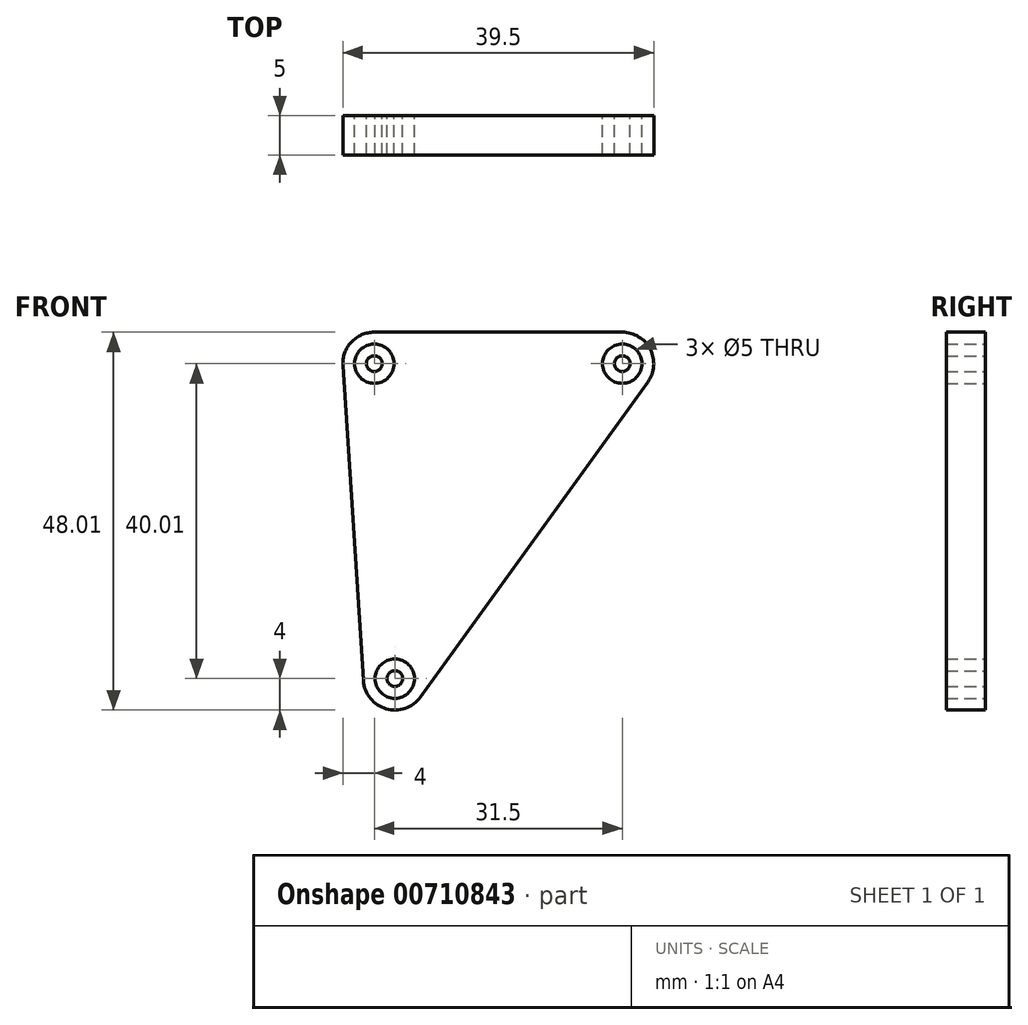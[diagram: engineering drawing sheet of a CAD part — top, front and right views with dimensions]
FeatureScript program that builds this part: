
annotation { "Feature Type Name" : "Feature", "Feature Type Description" : "" }
export const myFeature = defineFeature(function(context is Context, id is Id, definition is map)
    precondition{}
    {
        {
            var Q0;
            Q0=qCreatedBy(makeId("Front.planeOp"),FACE);
            var sketch = newSketch(context, id + "F0", { "sketchPlane" : qUnion([Q0])});
            skCircle(sketch, "E0", {"center": v(-5.7, 2.74) * mm, "radius": 2.5 * mm});
            skCircle(sketch, "E1", {"center": v(25.79, 2.74) * mm, "radius": 2.5 * mm});
            skCircle(sketch, "E2", {"center": v(-3.1, -37.27) * mm, "radius": 2.5 * mm});
            skArc(sketch, "E3", {"start": v(-5.7, 6.74) * mm, "mid": v(-8.63, 5.47) * mm, "end": v(-9.7, 2.48) * mm});
            skArc(sketch, "E4", {"start": v(29.03, 0.4) * mm, "mid": v(29.35, 4.56) * mm, "end": v(25.79, 6.74) * mm});
            skArc(sketch, "E5", {"start": v(-7.1, -37.53) * mm, "mid": v(-4.2, -41.11) * mm, "end": v(0.14, -39.61) * mm});
            skCircle(sketch, "E6", {"center": v(-5.7, 2.74) * mm, "radius": 1 * mm});
            skCircle(sketch, "E7", {"center": v(-3.1, -37.27) * mm, "radius": 1 * mm});
            skCircle(sketch, "E8", {"center": v(25.79, 2.74) * mm, "radius": 1 * mm});
            skLineSegment(sketch, "E9", {"start": v(-9.7, 2.48) * mm, "end": v(-7.1, -37.53) * mm});
            skLineSegment(sketch, "E10", {"start": v(-5.71, 6.74) * mm, "end": v(25.79, 6.74) * mm});
            skLineSegment(sketch, "E11", {"start": v(29.03, 0.4) * mm, "end": v(0.14, -39.61) * mm});
            skSolve(sketch);
        }
        {
            var Q0;
            Q0=makeQuery(id+"F0.imprint","IMPRINT",FACE,{"disambiguationData":[TD([[makeQuery(id+"F0.imprint","IMPRINT",EDGE,{"derivedFrom":sQuery(id+"F0.wireOp",EDGE,"E0")}),-1.0]])]});
            var Q1;
            Q1=makeQuery(id+"F0.imprint","IMPRINT",FACE,{"disambiguationData":[TD([[makeQuery(id+"F0.imprint","IMPRINT",EDGE,{"derivedFrom":sQuery(id+"F0.wireOp",EDGE,"E6")}),1.0]])]});
            var Q2;
            Q2=makeQuery(id+"F0.imprint","IMPRINT",FACE,{"disambiguationData":[TD([[makeQuery(id+"F0.imprint","IMPRINT",EDGE,{"derivedFrom":sQuery(id+"F0.wireOp",EDGE,"E8")}),1.0]])]});
            var Q3;
            Q3=makeQuery(id+"F0.imprint","IMPRINT",FACE,{"disambiguationData":[TD([[makeQuery(id+"F0.imprint","IMPRINT",EDGE,{"derivedFrom":sQuery(id+"F0.wireOp",EDGE,"E7")}),1.0]])]});
            extrude(context, id + "F1", {"entities" : qUnion([Q0, Q1, Q2, Q3]), "depth" : 5 * mm, "offsetDistance" : 25 * mm});
        }
    });
